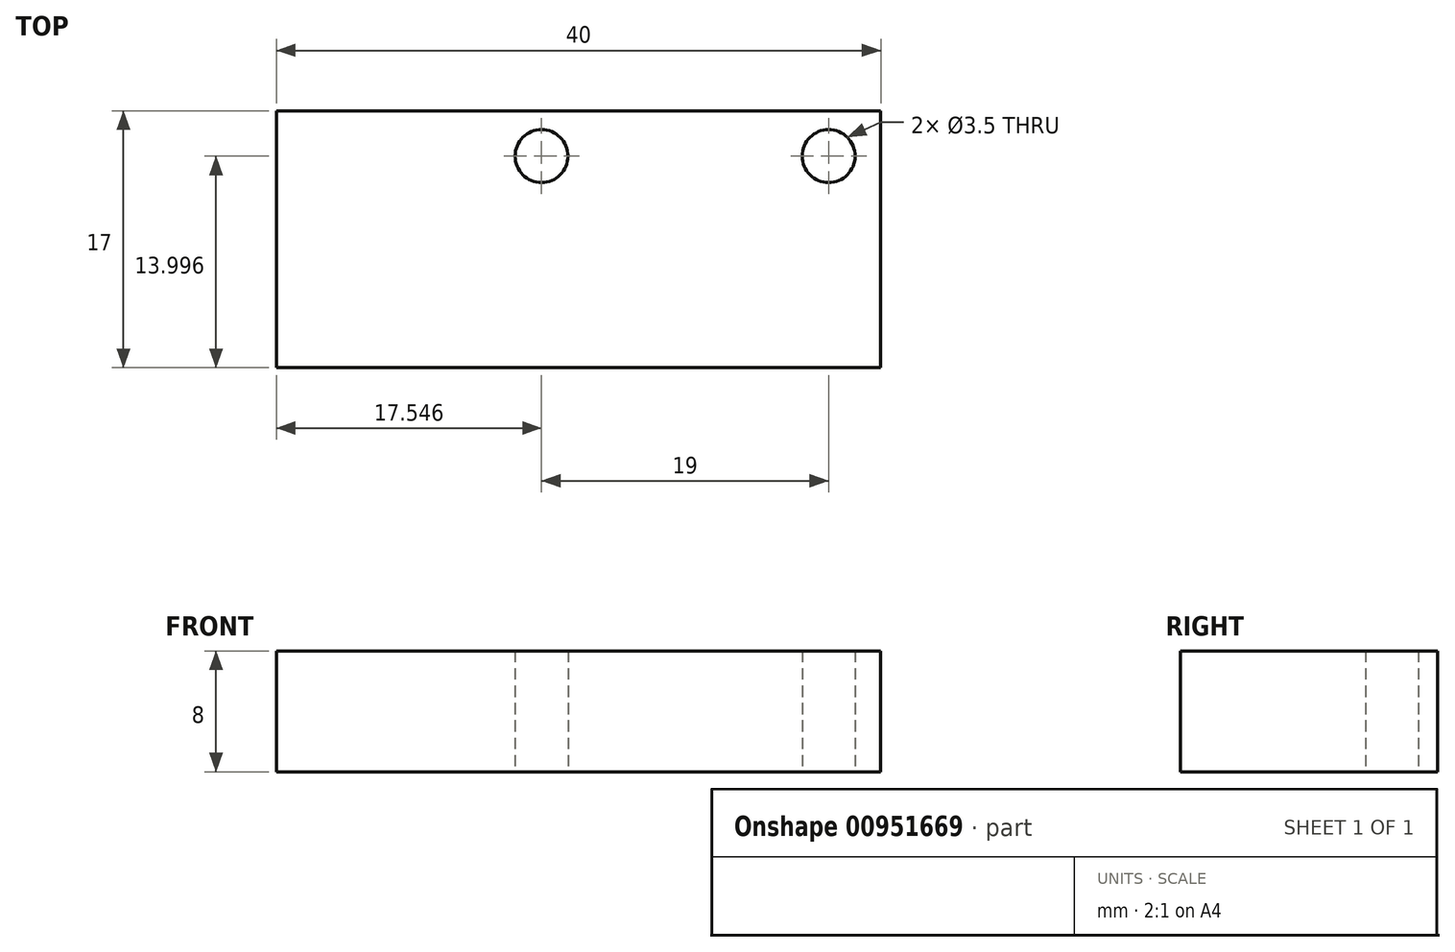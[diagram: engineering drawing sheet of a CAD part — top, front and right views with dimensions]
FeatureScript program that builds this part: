
annotation { "Feature Type Name" : "Feature", "Feature Type Description" : "" }
export const myFeature = defineFeature(function(context is Context, id is Id, definition is map)
    precondition{}
    {
        {
            var Q0;
            Q0=qCreatedBy(makeId("Top.planeOp"),FACE);
            var sketch = newSketch(context, id + "F0", { "sketchPlane" : qUnion([Q0])});
            skPoint(sketch, "E0.middle", {"position": v(0, 0) * mm});
            skCircle(sketch, "E1", {"center": v(15.84, -0.05) * mm, "radius": 1.75 * mm});
            skCircle(sketch, "E2", {"center": v(-3.16, -0.05) * mm, "radius": 1.75 * mm});
            skLineSegment(sketch, "E3.left", {"start": v(19.29, 2.95) * mm, "end": v(19.29, -14.05) * mm});
            skLineSegment(sketch, "E4.right", {"start": v(-20.71, -14.05) * mm, "end": v(-20.71, 2.95) * mm});
            skLineSegment(sketch, "E5", {"start": v(-20.71, 2.95) * mm, "end": v(19.29, 2.95) * mm});
            skLineSegment(sketch, "E6", {"start": v(-20.71, -14.05) * mm, "end": v(19.29, -14.05) * mm});
            skSolve(sketch);
        }
        {
            var Q0;
            Q0=makeQuery(id+"F0.imprint","IMPRINT",FACE,{"disambiguationData":[TD([[makeQuery(id+"F0.imprint","IMPRINT",EDGE,{"derivedFrom":sQuery(id+"F0.wireOp",EDGE,"E1")}),-1.0]])]});
            extrude(context, id + "F1", {"entities" : qUnion([Q0]), "depth" : 8 * mm, "offsetDistance" : 25 * mm});
        }
    });
